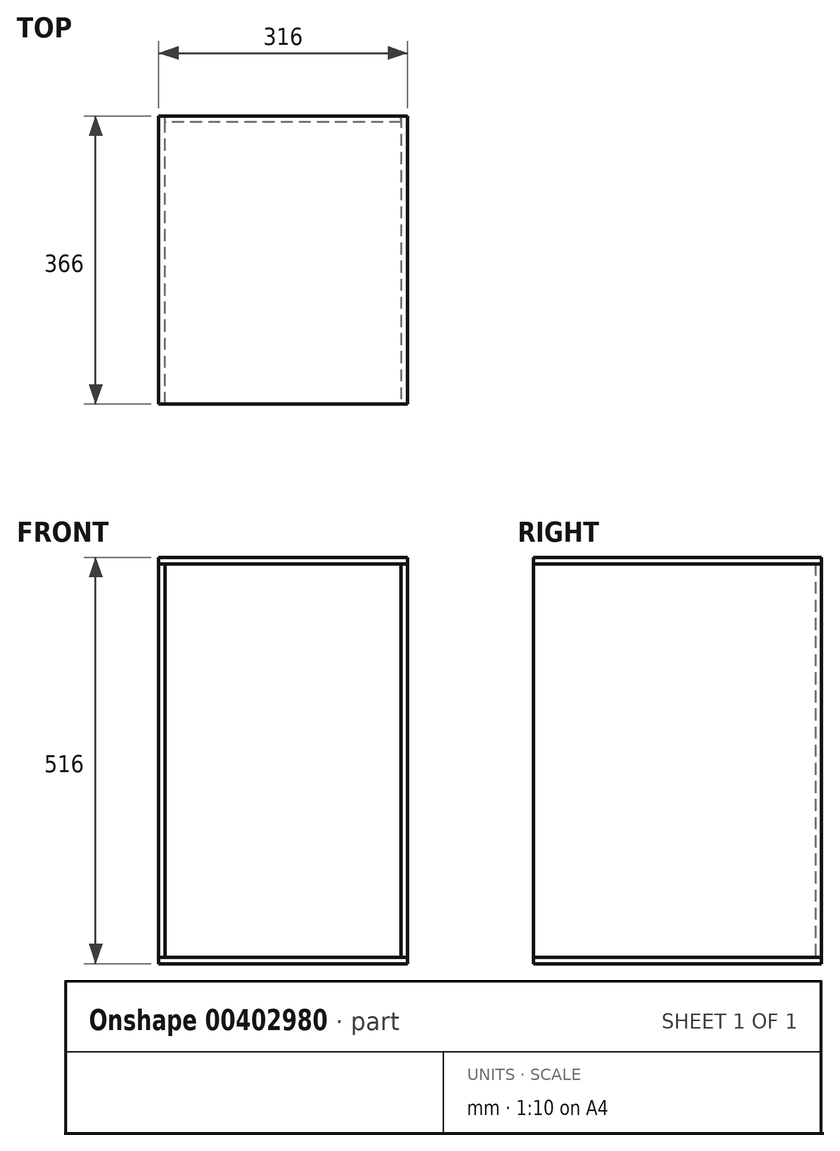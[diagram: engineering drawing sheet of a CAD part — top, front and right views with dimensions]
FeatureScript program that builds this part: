
annotation { "Feature Type Name" : "Feature", "Feature Type Description" : "" }
export const myFeature = defineFeature(function(context is Context, id is Id, definition is map)
    precondition{}
    {
        {
            assignVariable(context, id + "F0", {"name" : "wall_thickness", "anyValue" : 8});
        }
        {
            var Q0;
            Q0=qCreatedBy(makeId("Top.planeOp"),FACE);
            var sketch = newSketch(context, id + "F1", { "sketchPlane" : qUnion([Q0])});
            skLineSegment(sketch, "E0.bottom", {"start": v(158, 183) * mm, "end": v(-158, 183) * mm});
            skLineSegment(sketch, "E0.top", {"start": v(158, -183) * mm, "end": v(-158, -183) * mm});
            skLineSegment(sketch, "E0.left", {"start": v(158, 183) * mm, "end": v(158, -183) * mm});
            skLineSegment(sketch, "E0.right", {"start": v(-158, 183) * mm, "end": v(-158, -183) * mm});
            skPoint(sketch, "E0.middle", {"position": v(0, 0) * mm});
            skSolve(sketch);
        }
        {
            var Q0;
            Q0=makeQuery(id+"F1.imprint","IMPRINT",FACE,{"disambiguationData":[TD([[makeQuery(id+"F1.imprint","IMPRINT",EDGE,{"derivedFrom":sQuery(id+"F1.wireOp",EDGE,"E0.bottom")}),1.0]])]});
            extrude(context, id + "F2", {"entities" : qUnion([Q0]), "depth" : getVariable(context, 'wall_thickness') * mm});
        }
        {
            var Q0;
            Q0=makeQuery(id+"F2.opExtrude","SWEPT_FACE",FACE,{"disambiguationData":[OSD([sQuery(id+"F1.wireOp",EDGE,"E0.left")])]});
            var sketch = newSketch(context, id + "F3", { "sketchPlane" : qUnion([Q0])});
            skLineSegment(sketch, "E1.0", {"start": v(183, 8) * mm, "end": v(-183, 8) * mm});
            skLineSegment(sketch, "E2", {"start": v(-183, 8) * mm, "end": v(-183, 508) * mm});
            skLineSegment(sketch, "E3", {"start": v(-183, 508) * mm, "end": v(183, 508) * mm});
            skLineSegment(sketch, "E4", {"start": v(183, 508) * mm, "end": v(183, 8) * mm});
            skSolve(sketch);
        }
        {
            var Q0;
            Q0=makeQuery(id+"F3.imprint","IMPRINT",FACE,{"disambiguationData":[TD([[makeQuery(id+"F3.imprint","IMPRINT",EDGE,{"derivedFrom":sQuery(id+"F3.wireOp",EDGE,"E1.0")}),-1.0]])]});
            extrude(context, id + "F4", {"entities" : qUnion([Q0]), "oppositeDirection" : true, "depth" : getVariable(context, 'wall_thickness') * mm});
        }
        {
            var Q0;
            Q0=makeQuery(id+"F2.opExtrude","SWEPT_FACE",FACE,{"disambiguationData":[OSD([sQuery(id+"F1.wireOp",EDGE,"E0.right")])]});
            var sketch = newSketch(context, id + "F5", { "sketchPlane" : qUnion([Q0])});
            skLineSegment(sketch, "E5.0.0", {"start": v(-183, 508) * mm, "end": v(-183, 8) * mm});
            skLineSegment(sketch, "E5.0.1", {"start": v(-183, 8) * mm, "end": v(183, 8) * mm});
            skLineSegment(sketch, "E5.0.2", {"start": v(183, 8) * mm, "end": v(183, 508) * mm});
            skLineSegment(sketch, "E5.0.3", {"start": v(183, 508) * mm, "end": v(-183, 508) * mm});
            skSolve(sketch);
        }
        {
            var Q0;
            Q0=makeQuery(id+"F5.imprint","IMPRINT",FACE,{"disambiguationData":[TD([[makeQuery(id+"F5.imprint","IMPRINT",EDGE,{"derivedFrom":sQuery(id+"F5.wireOp",EDGE,"E5.0.0")}),1.0]])]});
            extrude(context, id + "F6", {"entities" : qUnion([Q0]), "oppositeDirection" : true, "depth" : (getVariable(context, 'wall_thickness')) * mm});
        }
        {
            var Q0;
            Q0=makeQuery(id+"F2.opExtrude","SWEPT_FACE",FACE,{"disambiguationData":[OSD([sQuery(id+"F1.wireOp",EDGE,"E0.bottom")])]});
            var sketch = newSketch(context, id + "F7", { "sketchPlane" : qUnion([Q0])});
            skLineSegment(sketch, "E6.0", {"start": v(-150, 508) * mm, "end": v(-150, 8) * mm});
            skLineSegment(sketch, "E6.1", {"start": v(-158, 8) * mm, "end": v(158, 8) * mm});
            skLineSegment(sketch, "E6.2", {"start": v(150, 508) * mm, "end": v(150, 8) * mm});
            skLineSegment(sketch, "E7", {"start": v(-150, 508) * mm, "end": v(150, 508) * mm});
            skSolve(sketch);
        }
        {
            var Q0;
            {var subQ0=sQuery(id+"F7.wireOp",EDGE,"E6.0");Q0=makeQuery(id+"F7.imprint","IMPRINT",FACE,{"disambiguationData":[TD([[makeQuery(id+"F7.imprint","IMPRINT",EDGE,{"derivedFrom":subQ0}),1.0]])]});}
            extrude(context, id + "F8", {"entities" : qUnion([Q0]), "oppositeDirection" : true, "depth" : getVariable(context, 'wall_thickness') * mm});
        }
        {
            var Q0;
            Q0=makeQuery(id+"F4.opExtrude","SWEPT_FACE",FACE,{"disambiguationData":[OSD([sQuery(id+"F3.wireOp",EDGE,"E3")])]});
            var sketch = newSketch(context, id + "F9", { "sketchPlane" : qUnion([Q0])});
            skPoint(sketch, "E8.0", {"position": v(158, 183) * mm});
            skPoint(sketch, "E8.1", {"position": v(-158, 183) * mm});
            skPoint(sketch, "E8.2", {"position": v(-158, -183) * mm});
            skPoint(sketch, "E8.3", {"position": v(158, -183) * mm});
            skLineSegment(sketch, "E9", {"start": v(-158, 183) * mm, "end": v(158, 183) * mm});
            skLineSegment(sketch, "E10", {"start": v(158, -183) * mm, "end": v(158, 183) * mm});
            skLineSegment(sketch, "E11", {"start": v(158, -183) * mm, "end": v(-158, -183) * mm});
            skLineSegment(sketch, "E12", {"start": v(-158, -183) * mm, "end": v(-158, 183) * mm});
            skSolve(sketch);
        }
        {
            var Q0;
            {var subQ2=sQuery(id+"F9.wireOp",EDGE,"E12");Q0=makeQuery(id+"F9.imprint","IMPRINT",FACE,{"disambiguationData":[TD([[makeQuery(id+"F9.imprint","IMPRINT",EDGE,{"derivedFrom":subQ2}),-1.0]])]});}
            var Q1;
            {var subQ0=sQuery(id+"F9.wireOp",EDGE,"E10");Q1=makeQuery(id+"F9.imprint","IMPRINT",FACE,{"disambiguationData":[TD([[makeQuery(id+"F9.imprint","IMPRINT",EDGE,{"derivedFrom":subQ0}),1.0]])]});}
            extrude(context, id + "F10", {"entities" : qUnion([Q0, Q1]), "depth" : (getVariable(context, 'wall_thickness')) * mm});
        }
    });
